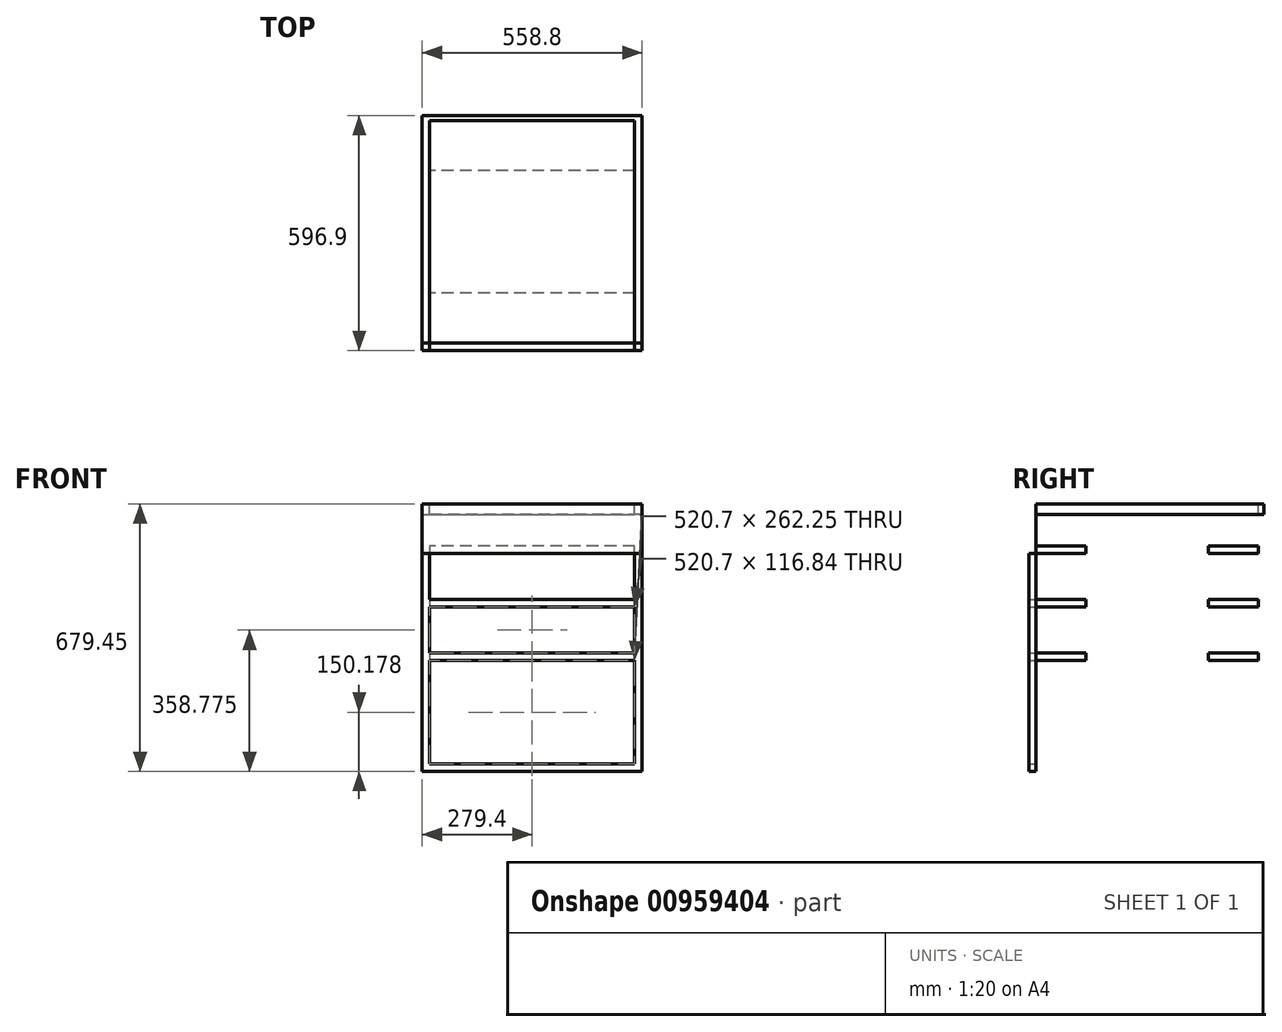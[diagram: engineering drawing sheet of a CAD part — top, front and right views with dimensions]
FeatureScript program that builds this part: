
annotation { "Feature Type Name" : "Feature", "Feature Type Description" : "" }
export const myFeature = defineFeature(function(context is Context, id is Id, definition is map)
    precondition{}
    {
        {
            assignVariable(context, id + "F0", {"name" : "depth", "anyValue" : 22.75});
        }
        {
            assignVariable(context, id + "F1", {"name" : "height", "anyValue" : 26.75});
        }
        {
            assignVariable(context, id + "F2", {"name" : "ply", "anyValue" : .75});
        }
        {
            assignVariable(context, id + "F3", {"name" : "back", "anyValue" : .5});
        }
        {
            var Q0;
            Q0=qCreatedBy(makeId("Top.planeOp"),FACE);
            var sketch = newSketch(context, id + "F4", { "sketchPlane" : qUnion([Q0])});
            skPoint(sketch, "E0.0", {"position": v(558.8, 508) * mm});
            skPoint(sketch, "E1.0", {"position": v(990.6, 0) * mm});
            skPoint(sketch, "E2.0", {"position": v(0, 577.85) * mm});
            skLineSegment(sketch, "E3.bottom", {"start": v(0, 577.85) * mm, "end": v(558.8, 577.85) * mm});
            skLineSegment(sketch, "E3.top", {"start": v(0, 565.15) * mm, "end": v(558.8, 565.15) * mm});
            skLineSegment(sketch, "E3.left", {"start": v(0, 577.85) * mm, "end": v(0, 565.15) * mm});
            skLineSegment(sketch, "E3.right", {"start": v(558.8, 577.85) * mm, "end": v(558.8, 565.15) * mm});
            skLineSegment(sketch, "E4.bottom", {"start": v(0, 565.15) * mm, "end": v(19.05, 565.15) * mm});
            skLineSegment(sketch, "E4.top", {"start": v(0, 0) * mm, "end": v(19.05, 0) * mm});
            skLineSegment(sketch, "E4.left", {"start": v(0, 565.15) * mm, "end": v(0, 0) * mm});
            skLineSegment(sketch, "E4.right", {"start": v(19.05, 565.15) * mm, "end": v(19.05, 0) * mm});
            skLineSegment(sketch, "E5.bottom", {"start": v(558.8, 565.15) * mm, "end": v(539.75, 565.15) * mm});
            skLineSegment(sketch, "E5.top", {"start": v(558.8, 0) * mm, "end": v(539.75, 0) * mm});
            skLineSegment(sketch, "E5.left", {"start": v(558.8, 565.15) * mm, "end": v(558.8, 0) * mm});
            skLineSegment(sketch, "E5.right", {"start": v(539.75, 565.15) * mm, "end": v(539.75, 0) * mm});
            skSolve(sketch);
        }
        {
            var Q0;
            Q0=qSketchRegion(id+"F4",true);
            extrude(context, id + "F5", {"entities" : qUnion([Q0]), "oppositeDirection" : true, "depth" : (getVariable(context, 'height')) * mm, "offsetDistance" : 25.4 * mm});
        }
        {
            var Q0;
            Q0=qCreatedBy(makeId("Top.planeOp"),FACE);
            var sketch = newSketch(context, id + "F6", { "sketchPlane" : qUnion([Q0])});
            skPoint(sketch, "E6.0", {"position": v(539.75, 0) * mm});
            skPoint(sketch, "E7.0", {"position": v(19.05, 565.15) * mm});
            skLineSegment(sketch, "E8.bottom", {"start": v(19.05, 565.15) * mm, "end": v(539.75, 565.15) * mm});
            skLineSegment(sketch, "E8.top", {"start": v(19.05, 0) * mm, "end": v(539.75, 0) * mm});
            skLineSegment(sketch, "E8.left", {"start": v(19.05, 565.15) * mm, "end": v(19.05, 0) * mm});
            skLineSegment(sketch, "E8.right", {"start": v(539.75, 565.15) * mm, "end": v(539.75, 0) * mm});
            skSolve(sketch);
        }
        {
            var Q0;
            Q0=qSketchRegion(id+"F6",true);
            extrude(context, id + "F7", {"entities" : qUnion([Q0]), "oppositeDirection" : true, "depth" : (getVariable(context, 'ply')) * mm, "offsetDistance" : 25.4 * mm});
        }
        {
            var Q0;
            Q0=makeQuery(id+"F5.opExtrude","CAP_FACE",FACE,{"disambiguationData":[OSD([sQuery(id+"F4.wireOp",EDGE,"E3.bottom"),sQuery(id+"F4.wireOp",EDGE,"E3.top"),sQuery(id+"F4.wireOp",EDGE,"E3.left"),sQuery(id+"F4.wireOp",EDGE,"E3.right"),sQuery(id+"F4.wireOp",EDGE,"E4.top"),sQuery(id+"F4.wireOp",EDGE,"E4.left"),sQuery(id+"F4.wireOp",EDGE,"E4.right"),sQuery(id+"F4.wireOp",EDGE,"E5.top"),sQuery(id+"F4.wireOp",EDGE,"E5.left"),sQuery(id+"F4.wireOp",EDGE,"E5.right")])],"isStart":false});
            var sketch = newSketch(context, id + "F8", { "sketchPlane" : qUnion([Q0])});
            skPoint(sketch, "E9.0", {"position": v(19.05, 0) * mm});
            skPoint(sketch, "E10.0", {"position": v(539.75, -565.15) * mm});
            skLineSegment(sketch, "E11.bottom", {"start": v(19.05, 0) * mm, "end": v(539.75, 0) * mm});
            skLineSegment(sketch, "E11.top", {"start": v(19.05, -565.15) * mm, "end": v(539.75, -565.15) * mm});
            skLineSegment(sketch, "E11.left", {"start": v(19.05, 0) * mm, "end": v(19.05, -565.15) * mm});
            skLineSegment(sketch, "E11.right", {"start": v(539.75, 0) * mm, "end": v(539.75, -565.15) * mm});
            skSolve(sketch);
        }
        {
            var Q0;
            Q0=qSketchRegion(id+"F8",true);
            extrude(context, id + "F9", {"entities" : qUnion([Q0]), "oppositeDirection" : true, "depth" : (getVariable(context, 'ply')) * mm, "offsetDistance" : 25.4 * mm});
        }
        {
            var Q0;
            Q0=makeQuery(id+"F5.opExtrude","SWEPT_FACE",FACE,{"disambiguationData":[OSD([sQuery(id+"F4.wireOp",EDGE,"E4.top")])]});
            var sketch = newSketch(context, id + "F10", { "sketchPlane" : qUnion([Q0])});
            skLineSegment(sketch, "E12.0", {"start": v(558.8, -679.45) * mm, "end": v(558.8, 0) * mm, "construction": true});
            skLineSegment(sketch, "E13.bottom", {"start": v(0, 0) * mm, "end": v(558.8, 0) * mm});
            skLineSegment(sketch, "E13.top", {"start": v(0, -135.73) * mm, "end": v(558.8, -135.73) * mm});
            skLineSegment(sketch, "E13.left", {"start": v(0, 0) * mm, "end": v(0, -135.73) * mm});
            skLineSegment(sketch, "E13.right", {"start": v(558.8, 0) * mm, "end": v(558.8, -135.73) * mm});
            skSolve(sketch);
        }
        {
            var Q0;
            Q0=qSketchRegion(id+"F10",true);
            extrude(context, id + "F11", {"entities" : qUnion([Q0]), "depth" : 19.05 * mm, "offsetDistance" : 25.4 * mm});
        }
        {
            var Q0;
            Q0=makeQuery(id+"F5.opExtrude","SWEPT_FACE",FACE,{"disambiguationData":[OSD([sQuery(id+"F4.wireOp",EDGE,"E3.top")])]});
            var sketch = newSketch(context, id + "F12", { "sketchPlane" : qUnion([Q0])});
            skLineSegment(sketch, "E14.0", {"start": v(19.05, -660.4) * mm, "end": v(539.75, -660.4) * mm, "construction": true});
            skLineSegment(sketch, "E15.0", {"start": v(19.05, -679.45) * mm, "end": v(19.05, 0) * mm, "construction": true});
            skLineSegment(sketch, "E16.0", {"start": v(539.75, -679.45) * mm, "end": v(539.75, 0) * mm, "construction": true});
            skLineSegment(sketch, "E17.bottom", {"start": v(19.05, -358.78) * mm, "end": v(539.75, -358.78) * mm});
            skLineSegment(sketch, "E17.top", {"start": v(19.05, -339.73) * mm, "end": v(539.75, -339.73) * mm});
            skLineSegment(sketch, "E17.left", {"start": v(19.05, -358.78) * mm, "end": v(19.05, -339.73) * mm});
            skLineSegment(sketch, "E17.right", {"start": v(539.75, -358.78) * mm, "end": v(539.75, -339.73) * mm});
            skLineSegment(sketch, "E18.0", {"start": v(0, 0) * mm, "end": v(558.8, 0) * mm, "construction": true});
            skSolve(sketch);
        }
        {
            var Q0;
            Q0=qSketchRegion(id+"F12",true);
            extrude(context, id + "F13", {"entities" : qUnion([Q0]), "depth" : (getVariable(context, 'depth') - getVariable(context, 'back')) * mm, "offsetDistance" : 25.4 * mm});
        }
        {
            var Q0;
            Q0=makeQuery(id+"F5.opExtrude","SWEPT_FACE",FACE,{"disambiguationData":[OSD([sQuery(id+"F4.wireOp",EDGE,"E5.top")])]});
            var sketch = newSketch(context, id + "F14", { "sketchPlane" : qUnion([Q0])});
            skLineSegment(sketch, "E19.0.1", {"start": v(539.75, -135.73) * mm, "end": v(539.75, -339.73) * mm});
            skLineSegment(sketch, "E19.0.2", {"start": v(539.75, -679.45) * mm, "end": v(558.8, -679.45) * mm});
            skLineSegment(sketch, "E19.0.3", {"start": v(558.8, -679.45) * mm, "end": v(558.8, -135.73) * mm});
            skLineSegment(sketch, "E20.0.0", {"start": v(539.75, -339.73) * mm, "end": v(19.05, -339.73) * mm});
            skLineSegment(sketch, "E20.0.2", {"start": v(19.05, -358.78) * mm, "end": v(539.75, -358.78) * mm});
            skLineSegment(sketch, "E20.0.3", {"start": v(539.75, -358.78) * mm, "end": v(539.75, -339.73) * mm});
            skLineSegment(sketch, "E21.0.1", {"start": v(0, -135.73) * mm, "end": v(0, -679.45) * mm});
            skLineSegment(sketch, "E21.0.2", {"start": v(0, -679.45) * mm, "end": v(19.05, -679.45) * mm});
            skLineSegment(sketch, "E21.0.3", {"start": v(19.05, -660.4) * mm, "end": v(19.05, -358.78) * mm});
            skLineSegment(sketch, "E22.0.0", {"start": v(19.05, -679.45) * mm, "end": v(539.75, -679.45) * mm});
            skLineSegment(sketch, "E22.0.1", {"start": v(539.75, -679.45) * mm, "end": v(539.75, -660.4) * mm});
            skLineSegment(sketch, "E22.0.2", {"start": v(539.75, -660.4) * mm, "end": v(19.05, -660.4) * mm});
            skLineSegment(sketch, "E23.trimOffspring", {"start": v(539.75, -358.78) * mm, "end": v(539.75, -660.4) * mm});
            skLineSegment(sketch, "E24.trimOffspring", {"start": v(19.05, -339.73) * mm, "end": v(19.05, -135.73) * mm});
            skLineSegment(sketch, "E25.0", {"start": v(0, -135.73) * mm, "end": v(19.05, -135.73) * mm});
            skLineSegment(sketch, "E26.trimOffspring", {"start": v(539.75, -135.73) * mm, "end": v(558.8, -135.73) * mm});
            skSolve(sketch);
        }
        {
            var Q0;
            Q0=qSketchRegion(id+"F14",true);
            extrude(context, id + "F15", {"entities" : qUnion([Q0]), "depth" : 19.05 * mm, "offsetDistance" : 25.4 * mm});
        }
        {
            var Q0;
            Q0=makeQuery(id+"F15.opExtrude","SWEPT_BODY",BODY,{"disambiguationData":[OSD([sQuery(id+"F14.wireOp",EDGE,"E19.0.1"),sQuery(id+"F14.wireOp",EDGE,"E19.0.2"),sQuery(id+"F14.wireOp",EDGE,"E19.0.3"),sQuery(id+"F14.wireOp",EDGE,"E20.0.0"),sQuery(id+"F14.wireOp",EDGE,"E20.0.2"),sQuery(id+"F14.wireOp",EDGE,"E21.0.1"),sQuery(id+"F14.wireOp",EDGE,"E21.0.2"),sQuery(id+"F14.wireOp",EDGE,"E21.0.3"),sQuery(id+"F14.wireOp",EDGE,"E22.0.0"),sQuery(id+"F14.wireOp",EDGE,"E22.0.2"),sQuery(id+"F14.wireOp",EDGE,"E23.trimOffspring"),sQuery(id+"F14.wireOp",EDGE,"E24.trimOffspring"),sQuery(id+"F14.wireOp",EDGE,"E25.0"),sQuery(id+"F14.wireOp",EDGE,"E26.trimOffspring")])]});
            deleteBodies(context, id + "F16", {"entities" : qUnion([Q0])});
        }
        {
            var Q0;
            Q0=makeQuery(id+"F11.opExtrude","SWEPT_BODY",BODY,{"disambiguationData":[OSD([sQuery(id+"F10.wireOp",EDGE,"E13.bottom"),sQuery(id+"F10.wireOp",EDGE,"E13.top"),sQuery(id+"F10.wireOp",EDGE,"E13.left"),sQuery(id+"F10.wireOp",EDGE,"E13.right")])]});
            deleteBodies(context, id + "F17", {"entities" : qUnion([Q0])});
        }
        {
            var Q0;
            Q0=makeQuery(id+"F13.opExtrude","SWEPT_BODY",BODY,{"disambiguationData":[OSD([sQuery(id+"F12.wireOp",EDGE,"E17.bottom"),sQuery(id+"F12.wireOp",EDGE,"E17.top"),sQuery(id+"F12.wireOp",EDGE,"E17.left"),sQuery(id+"F12.wireOp",EDGE,"E17.right")])]});
            deleteBodies(context, id + "F18", {"entities" : qUnion([Q0])});
        }
        {
            var Q0;
            Q0=makeQuery(id+"F5.opExtrude","SWEPT_FACE",FACE,{"disambiguationData":[OSD([sQuery(id+"F4.wireOp",EDGE,"E4.right")])]});
            var sketch = newSketch(context, id + "F19", { "sketchPlane" : qUnion([Q0])});
            skLineSegment(sketch, "E27.bottom", {"start": v(438.15, -107.32) * mm, "end": v(565.15, -107.32) * mm});
            skLineSegment(sketch, "E27.top", {"start": v(438.15, -126.37) * mm, "end": v(565.15, -126.37) * mm});
            skLineSegment(sketch, "E27.left", {"start": v(438.15, -107.32) * mm, "end": v(438.15, -126.37) * mm});
            skLineSegment(sketch, "E27.right", {"start": v(565.15, -107.32) * mm, "end": v(565.15, -126.37) * mm});
            skLineSegment(sketch, "E28.bottom", {"start": v(0, -107.32) * mm, "end": v(127, -107.32) * mm});
            skLineSegment(sketch, "E28.top", {"start": v(0, -126.37) * mm, "end": v(127, -126.37) * mm});
            skLineSegment(sketch, "E28.left", {"start": v(0, -107.32) * mm, "end": v(0, -126.37) * mm});
            skLineSegment(sketch, "E28.right", {"start": v(127, -107.32) * mm, "end": v(127, -126.37) * mm});
            skLineSegment(sketch, "E29.bottom", {"start": v(0, -243.2) * mm, "end": v(127, -243.2) * mm});
            skLineSegment(sketch, "E29.top", {"start": v(0, -262.25) * mm, "end": v(127, -262.25) * mm});
            skLineSegment(sketch, "E29.left", {"start": v(0, -243.2) * mm, "end": v(0, -262.25) * mm});
            skLineSegment(sketch, "E29.right", {"start": v(127, -243.2) * mm, "end": v(127, -262.25) * mm});
            skLineSegment(sketch, "E30.bottom", {"start": v(438.15, -243.2) * mm, "end": v(565.15, -243.2) * mm});
            skLineSegment(sketch, "E30.top", {"start": v(438.15, -262.25) * mm, "end": v(565.15, -262.25) * mm});
            skLineSegment(sketch, "E30.left", {"start": v(438.15, -243.2) * mm, "end": v(438.15, -262.25) * mm});
            skLineSegment(sketch, "E30.right", {"start": v(565.15, -243.2) * mm, "end": v(565.15, -262.25) * mm});
            skLineSegment(sketch, "E31.bottom", {"start": v(0, -379.1) * mm, "end": v(127, -379.1) * mm});
            skLineSegment(sketch, "E31.top", {"start": v(0, -398.15) * mm, "end": v(127, -398.15) * mm});
            skLineSegment(sketch, "E31.left", {"start": v(0, -379.1) * mm, "end": v(0, -398.15) * mm});
            skLineSegment(sketch, "E31.right", {"start": v(127, -379.1) * mm, "end": v(127, -398.15) * mm});
            skLineSegment(sketch, "E32.bottom", {"start": v(438.15, -379.1) * mm, "end": v(565.15, -379.1) * mm});
            skLineSegment(sketch, "E32.top", {"start": v(438.15, -398.15) * mm, "end": v(565.15, -398.15) * mm});
            skLineSegment(sketch, "E32.left", {"start": v(438.15, -379.1) * mm, "end": v(438.15, -398.15) * mm});
            skLineSegment(sketch, "E32.right", {"start": v(565.15, -379.1) * mm, "end": v(565.15, -398.15) * mm});
            skSolve(sketch);
        }
        {
            var Q0;
            Q0=qSketchRegion(id+"F19",true);
            var Q1;
            Q1=makeQuery(id+"F5.opExtrude","SWEPT_FACE",FACE,{"disambiguationData":[OSD([sQuery(id+"F4.wireOp",EDGE,"E5.right")])]});
            extrude(context, id + "F20", {"entities" : qUnion([Q0]), "endBound" : BoundingType.UP_TO_SURFACE, "depth" : 91.44 * mm, "endBoundEntityFace" : qUnion([Q1]), "offsetDistance" : 25.4 * mm});
        }
        {
            var Q0;
            Q0=qCreatedBy(makeId("Front.planeOp"),FACE);
            var sketch = newSketch(context, id + "F21", { "sketchPlane" : qUnion([Q0])});
            skLineSegment(sketch, "E33.0", {"start": v(558.8, -679.45) * mm, "end": v(558.8, 0) * mm});
            skLineSegment(sketch, "E34.bottom", {"start": v(0, 0) * mm, "end": v(558.8, 0) * mm});
            skLineSegment(sketch, "E34.top", {"start": v(0, -125.87) * mm, "end": v(558.8, -125.87) * mm});
            skLineSegment(sketch, "E34.left", {"start": v(0, 0) * mm, "end": v(0, -125.87) * mm});
            skLineSegment(sketch, "E34.right", {"start": v(558.8, 0) * mm, "end": v(558.8, -125.87) * mm});
            skSolve(sketch);
        }
        {
            var Q0;
            Q0=qSketchRegion(id+"F21",true);
            extrude(context, id + "F22", {"entities" : qUnion([Q0]), "depth" : (getVariable(context, 'ply')) * mm, "offsetDistance" : 25.4 * mm});
        }
        {
            var Q0;
            Q0=qCreatedBy(makeId("Front.planeOp"),FACE);
            var sketch = newSketch(context, id + "F23", { "sketchPlane" : qUnion([Q0])});
            skLineSegment(sketch, "E35.bottom", {"start": v(207.48, -160.99) * mm, "end": v(470.98, -160.99) * mm});
            skLineSegment(sketch, "E35.top", {"start": v(207.48, -234.9) * mm, "end": v(470.98, -234.9) * mm});
            skLineSegment(sketch, "E35.left", {"start": v(207.48, -160.99) * mm, "end": v(207.48, -234.9) * mm});
            skLineSegment(sketch, "E35.right", {"start": v(470.98, -160.99) * mm, "end": v(470.98, -234.9) * mm});
            skSolve(sketch);
        }
        {
            var Q0;
            Q0=qSketchRegion(id+"F23",true);
            extrude(context, id + "F24", {"entities" : qUnion([Q0]), "depth" : 19.05 * mm, "offsetDistance" : 25.4 * mm});
        }
        {
            var Q0;
            Q0=makeQuery(id+"F9.opExtrude","SWEPT_FACE",FACE,{"disambiguationData":[OSD([sQuery(id+"F8.wireOp",EDGE,"E11.bottom")])]});
            var sketch = newSketch(context, id + "F25", { "sketchPlane" : qUnion([Q0])});
            skLineSegment(sketch, "E36.0", {"start": v(0, -125.87) * mm, "end": v(19.05, -125.87) * mm});
            skPoint(sketch, "E37.0", {"position": v(0, -679.45) * mm});
            skPoint(sketch, "E38.0", {"position": v(19.05, -660.4) * mm});
            skPoint(sketch, "E39.0", {"position": v(539.75, -660.4) * mm});
            skPoint(sketch, "E40.0", {"position": v(558.8, -679.45) * mm});
            skPoint(sketch, "E41.0", {"position": v(558.8, -125.87) * mm});
            skPoint(sketch, "E42.0", {"position": v(539.75, -243.2) * mm});
            skPoint(sketch, "E43.0", {"position": v(19.05, -243.2) * mm});
            skPoint(sketch, "E44.0", {"position": v(19.05, -262.25) * mm});
            skPoint(sketch, "E45.0", {"position": v(19.05, -379.1) * mm});
            skPoint(sketch, "E46.0", {"position": v(539.75, -398.15) * mm});
            skLineSegment(sketch, "E47.top", {"start": v(0, -679.45) * mm, "end": v(19.05, -679.45) * mm});
            skLineSegment(sketch, "E47.left", {"start": v(0, -125.87) * mm, "end": v(0, -679.45) * mm});
            skLineSegment(sketch, "E47.right", {"start": v(19.05, -125.87) * mm, "end": v(19.05, -243.2) * mm});
            skLineSegment(sketch, "E48.bottom", {"start": v(558.8, -125.87) * mm, "end": v(539.75, -125.87) * mm});
            skLineSegment(sketch, "E48.top", {"start": v(558.8, -679.45) * mm, "end": v(539.75, -679.45) * mm});
            skLineSegment(sketch, "E48.left", {"start": v(558.8, -125.87) * mm, "end": v(558.8, -679.45) * mm});
            skLineSegment(sketch, "E48.right", {"start": v(539.75, -125.87) * mm, "end": v(539.75, -379.1) * mm});
            skLineSegment(sketch, "E49.bottom", {"start": v(19.05, -243.2) * mm, "end": v(539.75, -243.2) * mm});
            skLineSegment(sketch, "E49.top", {"start": v(19.05, -262.25) * mm, "end": v(539.75, -262.25) * mm});
            skLineSegment(sketch, "E50.bottom", {"start": v(19.05, -379.1) * mm, "end": v(539.75, -379.1) * mm});
            skLineSegment(sketch, "E50.top", {"start": v(19.05, -398.15) * mm, "end": v(539.75, -398.15) * mm});
            skLineSegment(sketch, "E51.bottom", {"start": v(539.75, -679.45) * mm, "end": v(19.05, -679.45) * mm});
            skLineSegment(sketch, "E51.top", {"start": v(539.75, -660.4) * mm, "end": v(19.05, -660.4) * mm});
            skLineSegment(sketch, "E51.left", {"start": v(539.75, -679.45) * mm, "end": v(539.75, -660.4) * mm});
            skLineSegment(sketch, "E51.right", {"start": v(19.05, -679.45) * mm, "end": v(19.05, -660.4) * mm});
            skLineSegment(sketch, "E52.trimOffspring", {"start": v(539.75, -125.87) * mm, "end": v(558.8, -125.87) * mm});
            skLineSegment(sketch, "E53.trimOffspring", {"start": v(19.05, -398.15) * mm, "end": v(19.05, -679.45) * mm});
            skLineSegment(sketch, "E54.trimOffspring", {"start": v(19.05, -262.25) * mm, "end": v(19.05, -379.1) * mm});
            skLineSegment(sketch, "E55.trimOffspring", {"start": v(539.75, -398.15) * mm, "end": v(539.75, -679.45) * mm});
            skSolve(sketch);
        }
        {
            var Q0;
            Q0=qSketchRegion(id+"F25",true);
            extrude(context, id + "F26", {"entities" : qUnion([Q0]), "depth" : 19.05 * mm, "offsetDistance" : 25.4 * mm});
        }
        {
            var Q0;
            Q0=makeQuery(id+"F24.opExtrude","SWEPT_BODY",BODY,{"disambiguationData":[OSD([sQuery(id+"F23.wireOp",EDGE,"E35.bottom"),sQuery(id+"F23.wireOp",EDGE,"E35.top"),sQuery(id+"F23.wireOp",EDGE,"E35.left"),sQuery(id+"F23.wireOp",EDGE,"E35.right")])]});
            deleteBodies(context, id + "F27", {"entities" : qUnion([Q0])});
        }
    });
